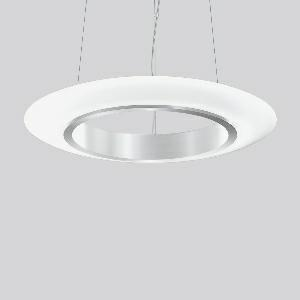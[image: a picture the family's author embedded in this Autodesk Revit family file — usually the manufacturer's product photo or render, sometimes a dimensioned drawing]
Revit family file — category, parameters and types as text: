
# Revit family: ring_of_fire_p_311570_004_1_76_1da4
name_source: partatom
category: Lighting Fixtures
units: mm (PartAtom-declared; Revit-internal decimal feet)

## family parameters
Cut with Voids When Loaded = No
Host = Face
Light Source = No
Part Type = Normal
Room Calculation Point = No
Round Connector Dimension = Use Diameter
Shared = No

## types (1)
- RING OF FIRE P (1 x LED Modul 840, 4150 lm, 4000)
    Apparent Load = 37 VA
    CIE Flux Codes = 43 73 90 55 100
    Color Rendering = 80
    Color Temperature = 4000
    Default Elevation = 1800 mm
    Description = Series: RING OF FIRE
A uniquely shaped pendant luminaire with elliptical glass. Supporting ring made of anodised aluminium. Canopy aluminium anodised. Opal glass: mouth-blown, satin finish. Suitable for pendant. 3-point steel cable suspension, steplessly adjustable. Special lengths available on request. For pendant lengths of up to 2 m, power is supplied through a suspension cable. For pendant lengths of 2 m and more, power must be supplied through a separate cable. Converter integrated in the canopy. TouchDim sensor capable. Light and/or presence sensors can be integrated. 
Colour: anodised aluminium
Diameter: 690 mm
Height: 81 mm
Suspension length: 500-1200 mm
Lamp: LED
Socket: without socket
Colour temperature: 4000K
Colour rendering index (CRI): 80
System power: 37 W
Rated luminous flux: 4150 lm
Luminous efficiency: 112 lm/W
Control gear: Converter, dimmable, DALI
Protection class: I
Type of protection: IP 20
    Height = 81 mm
    Lamp = 1 x LED Modul 840
    Lamp Light Flux = 4150 lm
    Lamp count = 1
    Length = 690 mm
    Lifetime = 50000 h
    Luminous efficacy = 112 lm/W
    Manufacturer = RZB
    ModVariant = No
    Model = 311570.004.1.76
    Mounting Place = Ceiling
    Mounting Type = Pendant
    Number of Poles = 1
    OnlyDefault = Yes
    Power Factor = 1
    Product Name = RING OF FIRE P
    Product group = Pendant luminaires
    ProductGroupID = 902
    Protection Class = Protection class I
    Protection Degree = IP 20
    RLX_Detail_Level = 1
    RLX_Emergency_Light_Flux = 0 lm
    RLX_Emergency_Type = 0
    RLX_Emergency_Type_DB = No
    RlxData = <blob elided: 30877 chars, md5=ecb518ec>
    Socket = socket
    Standby Power = 0 W
    System Light Flux = 4150 lm
    System Power = 37 W
    Type Comments = Product without accessories
    Type Image = 311570.004.jpg
    URL = http://relux.com
    VarID = ---
    Voltage = 230 V
    Voltage Range = 220-240 V
    Weight = 0.00 kg
    Width = 0 mm  [stored 0 ft]

note: [stored X ft] marks values corroborated as IEEE doubles in the binary element streams (Revit-internal decimal feet)

## geometry (parser evidence)
native form markers: Blend x4, Sweep x9
no freeform markers — native parametric forms only
